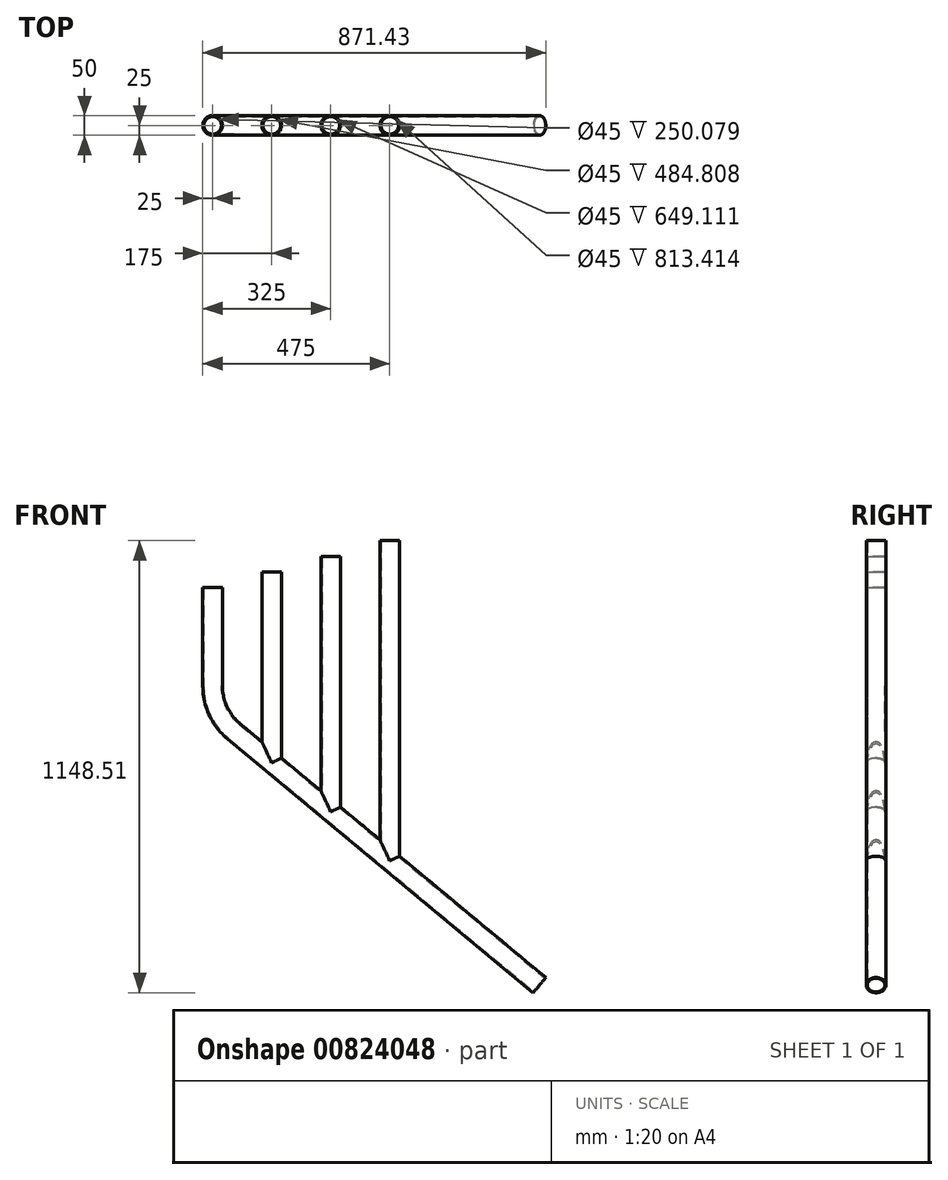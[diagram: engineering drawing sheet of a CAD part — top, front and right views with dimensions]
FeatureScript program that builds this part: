
annotation { "Feature Type Name" : "Feature", "Feature Type Description" : "" }
export const myFeature = defineFeature(function(context is Context, id is Id, definition is map)
    precondition{}
    {
        {
            var Q0;
            Q0=qCreatedBy(makeId("Front.planeOp"),FACE);
            var sketch = newSketch(context, id + "F0", { "sketchPlane" : qUnion([Q0])});
            skLineSegment(sketch, "E0", {"start": v(0, 584.73) * mm, "end": v(0, 334.65) * mm});
            skLineSegment(sketch, "E1", {"start": v(54.19, 219.24) * mm, "end": v(830.46, -425.24) * mm});
            skLineSegment(sketch, "E2", {"start": v(150, 624.5) * mm, "end": v(150, 139.7) * mm});
            skPoint(sketch, "E3.visualSharp", {"position": v(0, 264.22) * mm});
            skArc(sketch, "E3.filletArc", {"start": v(0, 334.65) * mm, "mid": v(14.22, 270.9) * mm, "end": v(54.19, 219.24) * mm});
            skLineSegment(sketch, "E4", {"start": v(0, 584.73) * mm, "end": v(1258.46, 918.4) * mm, "construction": true});
            skLineSegment(sketch, "E5", {"start": v(300, 664.27) * mm, "end": v(300, 15.16) * mm});
            skLineSegment(sketch, "E6", {"start": v(450, 704.04) * mm, "end": v(450, -109.37) * mm});
            skLineSegment(sketch, "E7", {"start": v(0, 584.73) * mm, "end": v(1380.1, 584.73) * mm, "construction": true});
            skSolve(sketch);
        }
        {
            var Q0;
            Q0=qCreatedBy(makeId("Top.planeOp"),FACE);
            var Q1;
            Q1=sQuery(id+"F0.wireOp",VERTEX,"E0.start");
            cPlane(context, id + "F1", {"entities" : qUnion([Q0, Q1]), "cplaneType" : CPlaneType.PLANE_POINT, "offset" : 25 * mm, "width" : 150 * mm, "height" : 150 * mm});
        }
        {
            var Q0;
            Q0=qCreatedBy(id+"F1.planeOp",FACE);
            var sketch = newSketch(context, id + "F2", { "sketchPlane" : qUnion([Q0])});
            skCircle(sketch, "E8", {"center": v(0, 0) * mm, "radius": 25 * mm});
            skSolve(sketch);
        }
        {
            var Q0;
            Q0=makeQuery(id+"F2.imprint","IMPRINT",FACE,{"disambiguationData":[TD([[makeQuery(id+"F2.imprint","IMPRINT",EDGE,{"derivedFrom":sQuery(id+"F2.wireOp",EDGE,"E8")}),1.0]])]});
            var Q1;
            Q1=sQuery(id+"F0.wireOp",EDGE,"E0");
            var Q2;
            Q2=sQuery(id+"F0.wireOp",EDGE,"E3.filletArc");
            var Q3;
            Q3=sQuery(id+"F0.wireOp",EDGE,"E1");
            sweep(context, id + "F3", {"profiles" : qUnion([Q0]), "path" : qUnion([Q1, Q2, Q3])});
        }
        {
            var Q0;
            Q0=qCreatedBy(makeId("Top.planeOp"),FACE);
            var Q1;
            Q1=sQuery(id+"F0.wireOp",VERTEX,"E2.start");
            cPlane(context, id + "F4", {"entities" : qUnion([Q0, Q1]), "cplaneType" : CPlaneType.PLANE_POINT, "offset" : 25 * mm, "width" : 150 * mm, "height" : 150 * mm});
        }
        {
            var Q0;
            Q0=qCreatedBy(makeId("Top.planeOp"),FACE);
            var Q1;
            Q1=sQuery(id+"F0.wireOp",VERTEX,"E5.start");
            cPlane(context, id + "F5", {"entities" : qUnion([Q0, Q1]), "cplaneType" : CPlaneType.PLANE_POINT, "offset" : 25 * mm, "width" : 150 * mm, "height" : 150 * mm});
        }
        {
            var Q0;
            Q0=qCreatedBy(makeId("Top.planeOp"),FACE);
            var Q1;
            Q1=sQuery(id+"F0.wireOp",VERTEX,"E6.start");
            cPlane(context, id + "F6", {"entities" : qUnion([Q0, Q1]), "cplaneType" : CPlaneType.PLANE_POINT, "offset" : 25 * mm, "width" : 150 * mm, "height" : 150 * mm});
        }
        {
            var Q0;
            Q0=qCreatedBy(id+"F4.planeOp",FACE);
            var sketch = newSketch(context, id + "F7", { "sketchPlane" : qUnion([Q0])});
            skCircle(sketch, "E9", {"center": v(150, 0) * mm, "radius": 25 * mm});
            skSolve(sketch);
        }
        {
            var Q0;
            Q0=qCreatedBy(id+"F5.planeOp",FACE);
            var sketch = newSketch(context, id + "F8", { "sketchPlane" : qUnion([Q0])});
            skCircle(sketch, "E10", {"center": v(300, 0) * mm, "radius": 25 * mm});
            skSolve(sketch);
        }
        {
            var Q0;
            Q0=qCreatedBy(id+"F6.planeOp",FACE);
            var sketch = newSketch(context, id + "F9", { "sketchPlane" : qUnion([Q0])});
            skCircle(sketch, "E11", {"center": v(450, 0) * mm, "radius": 25 * mm});
            skSolve(sketch);
        }
        {
            var Q0;
            Q0=makeQuery(id+"F7.imprint","IMPRINT",FACE,{"disambiguationData":[TD([[makeQuery(id+"F7.imprint","IMPRINT",EDGE,{"derivedFrom":sQuery(id+"F7.wireOp",EDGE,"E9")}),1.0]])]});
            var Q1;
            Q1=sQuery(id+"F0.wireOp",EDGE,"E2");
            sweep(context, id + "F10", {"operationType" : NewBodyOperationType.ADD, "profiles" : qUnion([Q0]), "path" : qUnion([Q1])});
        }
        {
            var Q0;
            Q0=makeQuery(id+"F8.imprint","IMPRINT",FACE,{"disambiguationData":[TD([[makeQuery(id+"F8.imprint","IMPRINT",EDGE,{"derivedFrom":sQuery(id+"F8.wireOp",EDGE,"E10")}),1.0]])]});
            var Q1;
            Q1=sQuery(id+"F0.wireOp",EDGE,"E5");
            sweep(context, id + "F11", {"operationType" : NewBodyOperationType.ADD, "profiles" : qUnion([Q0]), "path" : qUnion([Q1])});
        }
        {
            var Q0;
            Q0=makeQuery(id+"F9.imprint","IMPRINT",FACE,{"disambiguationData":[TD([[makeQuery(id+"F9.imprint","IMPRINT",EDGE,{"derivedFrom":sQuery(id+"F9.wireOp",EDGE,"E11")}),1.0]])]});
            var Q1;
            Q1=sQuery(id+"F0.wireOp",EDGE,"E6");
            sweep(context, id + "F12", {"operationType" : NewBodyOperationType.ADD, "profiles" : qUnion([Q0]), "path" : qUnion([Q1])});
        }
        {
            var Q0;
            Q0=makeQuery(id+"F3.opSweep","CAP_FACE",FACE,{"disambiguationData":[OSD([sQuery(id+"F0.wireOp",VERTEX,"E0.start"),sQuery(id+"F2.wireOp",EDGE,"E8")])],"isStart":true});
            var Q1;
            Q1=makeQuery(id+"F10.opSweep","CAP_FACE",FACE,{"disambiguationData":[OSD([sQuery(id+"F0.wireOp",VERTEX,"E2.start"),sQuery(id+"F7.wireOp",EDGE,"E9")])],"isStart":true});
            var Q2;
            Q2=makeQuery(id+"F11.opSweep","CAP_FACE",FACE,{"disambiguationData":[OSD([sQuery(id+"F0.wireOp",VERTEX,"E5.start"),sQuery(id+"F8.wireOp",EDGE,"E10")])],"isStart":true});
            var Q3;
            Q3=makeQuery(id+"F12.opSweep","CAP_FACE",FACE,{"disambiguationData":[OSD([sQuery(id+"F0.wireOp",VERTEX,"E6.start"),sQuery(id+"F9.wireOp",EDGE,"E11")])],"isStart":true});
            var Q4;
            Q4=makeQuery(id+"F3.opSweep","CAP_FACE",FACE,{"disambiguationData":[OSD([sQuery(id+"F0.wireOp",VERTEX,"E1.end"),sQuery(id+"F2.wireOp",EDGE,"E8")])],"isStart":false});
            shell(context, id + "F13", {"entities" : qUnion([Q0, Q1, Q2, Q3, Q4]), "thickness" : 2.5 * mm});
        }
    });
